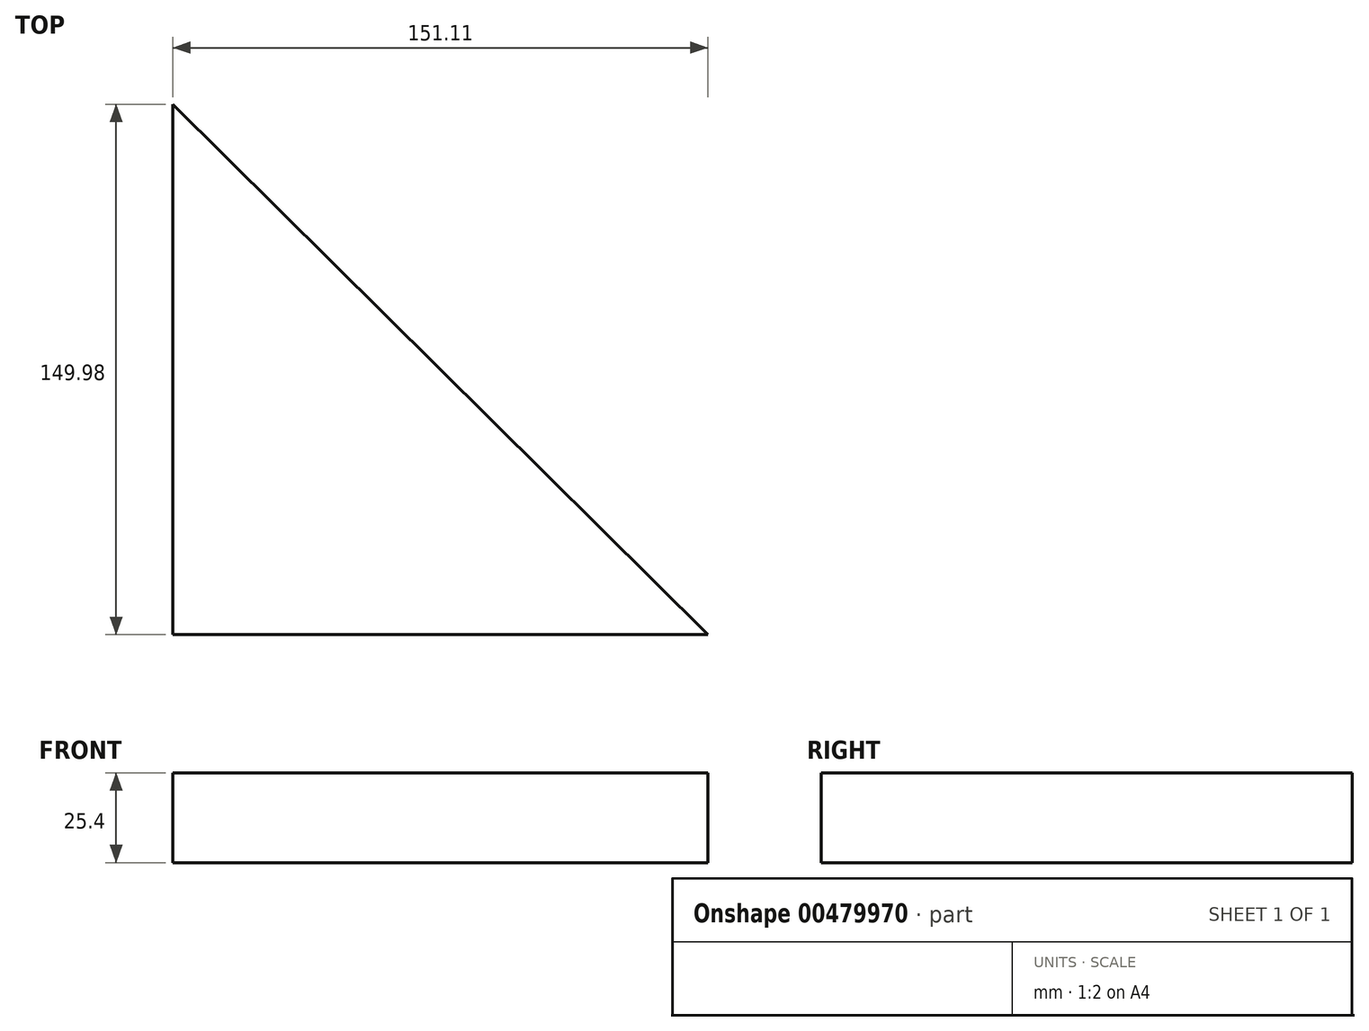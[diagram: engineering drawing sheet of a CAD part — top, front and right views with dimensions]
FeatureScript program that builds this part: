
annotation { "Feature Type Name" : "Feature", "Feature Type Description" : "" }
export const myFeature = defineFeature(function(context is Context, id is Id, definition is map)
    precondition{}
    {
        {
            var Q0;
            Q0=qCreatedBy(makeId("Top.planeOp"),FACE);
            var sketch = newSketch(context, id + "F0", { "sketchPlane" : qUnion([Q0])});
            skLineSegment(sketch, "E0", {"start": v(0, 0) * mm, "end": v(-74.77, -75.8) * mm});
            skLineSegment(sketch, "E1", {"start": v(76.34, -75.8) * mm, "end": v(-74.77, -75.8) * mm});
            skLineSegment(sketch, "E2", {"start": v(0, 0) * mm, "end": v(76.34, -75.8) * mm});
            skLineSegment(sketch, "E3", {"start": v(-74.77, -75.8) * mm, "end": v(-74.77, 74.17) * mm});
            skLineSegment(sketch, "E4", {"start": v(0, 0) * mm, "end": v(-74.77, 74.17) * mm});
            skSolve(sketch);
        }
        {
            var Q0;
            Q0 = qSketchRegion(id + "F0", true);
            extrude(context, id + "F1", {"entities" : qUnion([Q0]), "depth" : 25.4 * mm});
        }
    });
